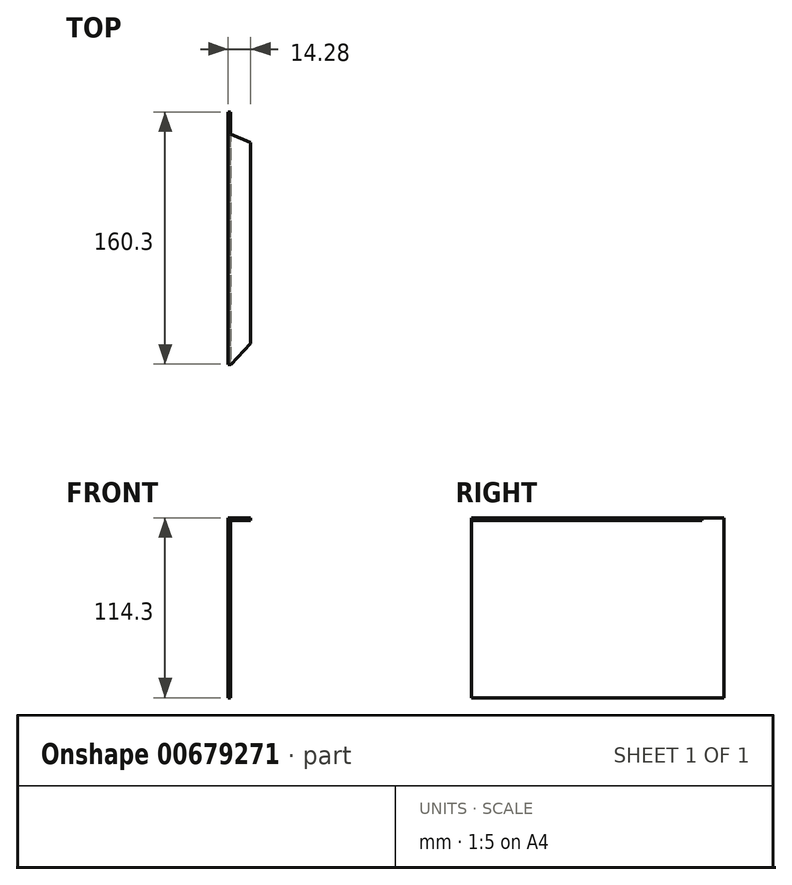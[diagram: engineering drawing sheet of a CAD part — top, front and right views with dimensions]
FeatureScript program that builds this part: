
annotation { "Feature Type Name" : "Feature", "Feature Type Description" : "" }
export const myFeature = defineFeature(function(context is Context, id is Id, definition is map)
    precondition{}
    {
        {
            var Q0;
            Q0=qCreatedBy(makeId("Top.planeOp"),FACE);
            var sketch = newSketch(context, id + "F0", { "sketchPlane" : qUnion([Q0])});
            skLineSegment(sketch, "E0.bottom", {"start": v(0.8, 80.15) * mm, "end": v(-0.8, 80.15) * mm});
            skLineSegment(sketch, "E0.top", {"start": v(0.8, -80.15) * mm, "end": v(-0.8, -80.15) * mm});
            skLineSegment(sketch, "E0.left", {"start": v(0.8, 80.15) * mm, "end": v(0.8, -80.15) * mm});
            skLineSegment(sketch, "E0.right", {"start": v(-0.8, 80.15) * mm, "end": v(-0.8, -80.15) * mm});
            skPoint(sketch, "E0.middle", {"position": v(0, 0) * mm});
            skLineSegment(sketch, "E1", {"start": v(-0.8, 80.15) * mm, "end": v(-0.8, 80.15) * mm});
            skLineSegment(sketch, "E2", {"start": v(-0.8, 80.15) * mm, "end": v(0.8, 80.15) * mm});
            skSolve(sketch);
        }
        {
            var Q0;
            Q0=qSketchRegion(id+"F0",true);
            extrude(context, id + "F1", {"entities" : qUnion([Q0]), "depth" : 114.3 * mm});
        }
        {
            var Q0;
            Q0=makeQuery(id+"F1.opExtrude","SWEPT_FACE",FACE,{"disambiguationData":[OSD([sQuery(id+"F0.wireOp",EDGE,"E0.left")])]});
            var sketch = newSketch(context, id + "F2", { "sketchPlane" : qUnion([Q0])});
            skPoint(sketch, "E3", {"position": v(65.66, 114.3) * mm});
            skPoint(sketch, "E4", {"position": v(-80.15, 114.3) * mm});
            skLineSegment(sketch, "E5.bottom", {"start": v(-80.15, 114.3) * mm, "end": v(65.66, 114.3) * mm});
            skLineSegment(sketch, "E5.top", {"start": v(-80.15, 112.71) * mm, "end": v(65.66, 112.71) * mm});
            skLineSegment(sketch, "E5.left", {"start": v(-80.15, 114.3) * mm, "end": v(-80.15, 112.71) * mm});
            skLineSegment(sketch, "E6.bottom", {"start": v(65.66, 112.71) * mm, "end": v(66.2, 112.71) * mm});
            skLineSegment(sketch, "E6.top", {"start": v(65.66, 114.3) * mm, "end": v(66.2, 114.3) * mm});
            skLineSegment(sketch, "E6.right", {"start": v(66.2, 112.71) * mm, "end": v(66.2, 114.3) * mm});
            skSolve(sketch);
        }
        {
            var Q0;
            Q0=qSketchRegion(id+"F2",true);
            extrude(context, id + "F3", {"entities" : qUnion([Q0]), "operationType" : NewBodyOperationType.ADD, "depth" : 12.7 * mm, "offsetDistance" : 25.4 * mm});
        }
        {
            var Q0;
            Q0=makeQuery(id+"F3.boolean.opBoolean","MERGE",FACE,{"derivedFrom":[makeQuery(id+"F1.opExtrude","CAP_FACE",FACE,{"disambiguationData":[OSD([sQuery(id+"F0.wireOp",EDGE,"E0.top"),sQuery(id+"F0.wireOp",EDGE,"E0.left"),sQuery(id+"F0.wireOp",EDGE,"E0.right"),sQuery(id+"F0.wireOp",EDGE,"E2")])],"isStart":false}),makeQuery(id+"F3.opExtrude","SWEPT_FACE",FACE,{"disambiguationData":[OSD([sQuery(id+"F2.wireOp",EDGE,"E5.bottom"),sQuery(id+"F2.wireOp",EDGE,"E6.top")])]})]});
            var sketch = newSketch(context, id + "F4", { "sketchPlane" : qUnion([Q0])});
            skLineSegment(sketch, "E7", {"start": v(0.8, 66.2) * mm, "end": v(13.5, 60.52) * mm});
            skLineSegment(sketch, "E8", {"start": v(13.5, 60.52) * mm, "end": v(13.5, 66.2) * mm});
            skLineSegment(sketch, "E9", {"start": v(13.5, 66.2) * mm, "end": v(0.8, 66.2) * mm});
            skLineSegment(sketch, "E10", {"start": v(0.92, -80.15) * mm, "end": v(13.5, -67.12) * mm});
            skLineSegment(sketch, "E11", {"start": v(13.5, -67.12) * mm, "end": v(13.5, -80.15) * mm});
            skLineSegment(sketch, "E12", {"start": v(13.5, -80.15) * mm, "end": v(0.92, -80.15) * mm});
            skSolve(sketch);
        }
        {
            var Q0;
            Q0 = qSketchRegion(id + "F4", true);
            extrude(context, id + "F5", {"entities" : qUnion([Q0]), "operationType" : NewBodyOperationType.REMOVE, "oppositeDirection" : true, "depth" : 25.4 * mm, "offsetDistance" : 25.4 * mm});
        }
    });
